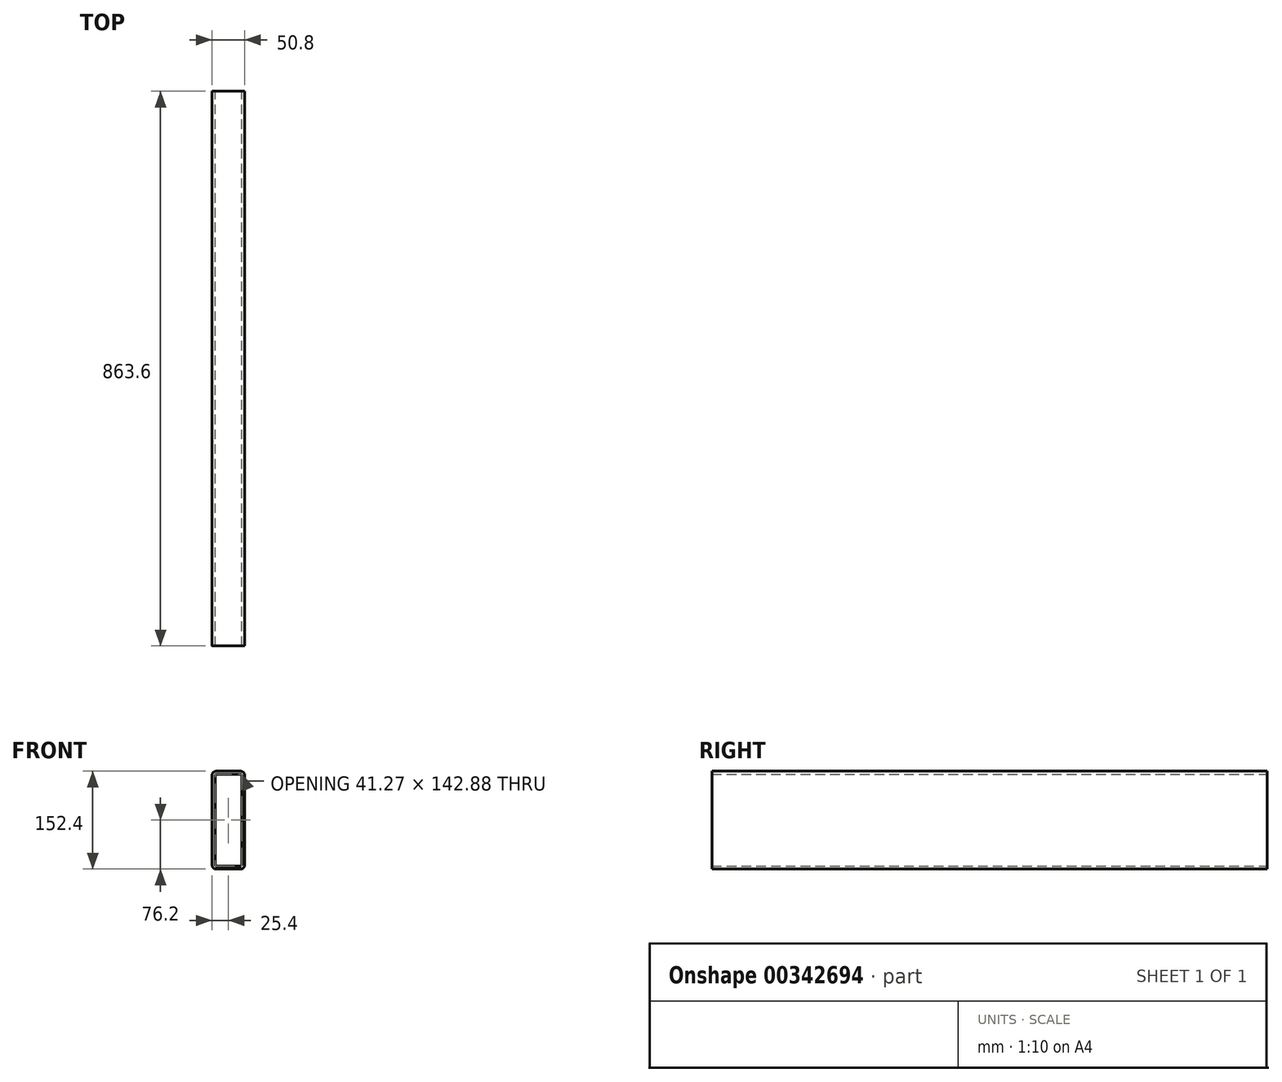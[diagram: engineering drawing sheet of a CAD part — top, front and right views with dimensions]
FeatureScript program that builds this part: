
annotation { "Feature Type Name" : "Feature", "Feature Type Description" : "" }
export const myFeature = defineFeature(function(context is Context, id is Id, definition is map)
    precondition{}
    {
        {
            var Q0;
            Q0=qCreatedBy(makeId("Front.planeOp"),FACE);
            var sketch = newSketch(context, id + "F0", { "sketchPlane" : qUnion([Q0])});
            skLineSegment(sketch, "E0.bottom", {"start": v(19.05, 76.2) * mm, "end": v(-19.05, 76.2) * mm});
            skLineSegment(sketch, "E0.top", {"start": v(19.05, -76.2) * mm, "end": v(-19.05, -76.2) * mm});
            skLineSegment(sketch, "E0.left", {"start": v(25.4, 69.85) * mm, "end": v(25.4, -69.85) * mm});
            skLineSegment(sketch, "E0.right", {"start": v(-25.4, 69.85) * mm, "end": v(-25.4, -69.85) * mm});
            skPoint(sketch, "E0.middle", {"position": v(0, 0) * mm});
            skPoint(sketch, "E1.visualSharp", {"position": v(-25.4, 76.2) * mm});
            skArc(sketch, "E1.filletArc", {"start": v(-19.05, 76.2) * mm, "mid": v(-23.54, 74.34) * mm, "end": v(-25.4, 69.85) * mm});
            skPoint(sketch, "E2.visualSharp", {"position": v(25.4, 76.2) * mm});
            skArc(sketch, "E2.filletArc", {"start": v(25.4, 69.85) * mm, "mid": v(23.54, 74.34) * mm, "end": v(19.05, 76.2) * mm});
            skPoint(sketch, "E3.visualSharp", {"position": v(25.4, -76.2) * mm});
            skArc(sketch, "E3.filletArc", {"start": v(19.05, -76.2) * mm, "mid": v(23.54, -74.34) * mm, "end": v(25.4, -69.85) * mm});
            skPoint(sketch, "E4.visualSharp", {"position": v(-25.4, -76.2) * mm});
            skArc(sketch, "E4.filletArc", {"start": v(-25.4, -69.85) * mm, "mid": v(-23.54, -74.34) * mm, "end": v(-19.05, -76.2) * mm});
            skLineSegment(sketch, "E5.0", {"start": v(-20.64, 69.85) * mm, "end": v(-20.64, -69.85) * mm});
            skLineSegment(sketch, "E5.1", {"start": v(19.05, 71.44) * mm, "end": v(-19.05, 71.44) * mm});
            skLineSegment(sketch, "E5.2", {"start": v(20.64, 69.85) * mm, "end": v(20.64, -69.85) * mm});
            skLineSegment(sketch, "E5.3", {"start": v(19.05, -71.44) * mm, "end": v(-19.05, -71.44) * mm});
            skPoint(sketch, "E6.visualSharp", {"position": v(-20.64, -71.44) * mm});
            skArc(sketch, "E6.filletArc", {"start": v(-20.64, -69.85) * mm, "mid": v(-20.17, -70.97) * mm, "end": v(-19.05, -71.44) * mm});
            skPoint(sketch, "E7.visualSharp", {"position": v(20.64, -71.44) * mm});
            skArc(sketch, "E7.filletArc", {"start": v(19.05, -71.44) * mm, "mid": v(20.17, -70.97) * mm, "end": v(20.64, -69.85) * mm});
            skPoint(sketch, "E8.visualSharp", {"position": v(20.64, 71.44) * mm});
            skArc(sketch, "E8.filletArc", {"start": v(20.64, 69.85) * mm, "mid": v(20.17, 70.97) * mm, "end": v(19.05, 71.44) * mm});
            skPoint(sketch, "E9.visualSharp", {"position": v(-20.64, 71.44) * mm});
            skArc(sketch, "E9.filletArc", {"start": v(-19.05, 71.44) * mm, "mid": v(-20.17, 70.97) * mm, "end": v(-20.64, 69.85) * mm});
            skSolve(sketch);
        }
        {
            var Q0;
            Q0=makeQuery(id+"F0.imprint","IMPRINT",FACE,{"disambiguationData":[TD([[makeQuery(id+"F0.imprint","IMPRINT",EDGE,{"derivedFrom":sQuery(id+"F0.wireOp",EDGE,"E0.bottom")}),1.0]])]});
            extrude(context, id + "F1", {"entities" : qUnion([Q0]), "depth" : 863.6 * mm});
        }
    });
